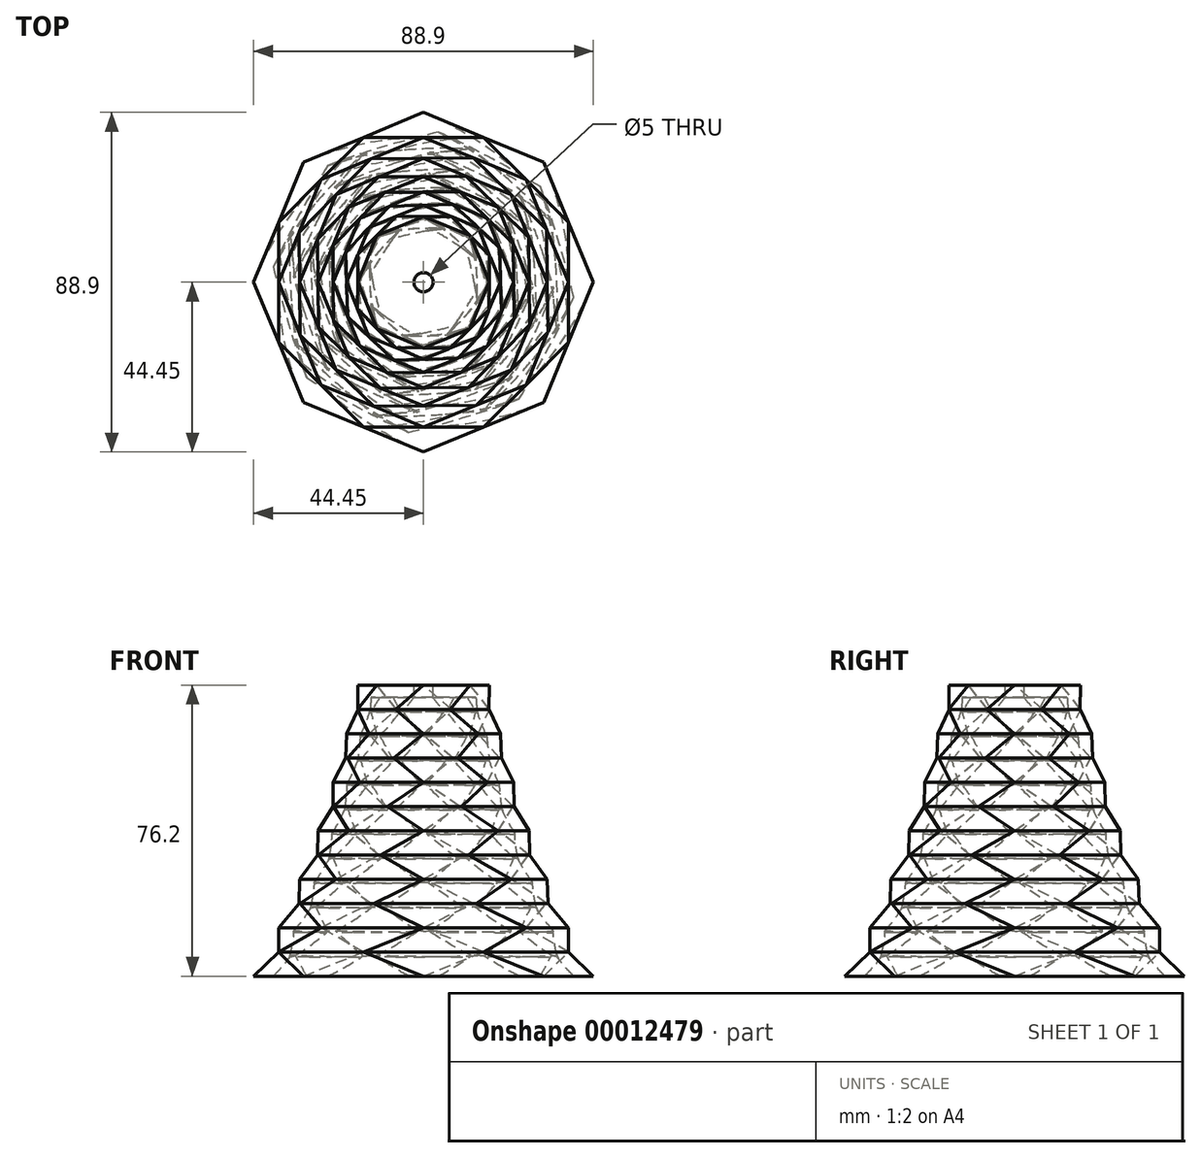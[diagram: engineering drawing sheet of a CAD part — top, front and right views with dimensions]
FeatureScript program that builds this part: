
annotation { "Feature Type Name" : "Feature", "Feature Type Description" : "" }
export const myFeature = defineFeature(function(context is Context, id is Id, definition is map)
    precondition{}
    {
        {
            var Q0;
            Q0=qCreatedBy(makeId("Top.planeOp"),FACE);
            var sketch = newSketch(context, id + "F0", { "sketchPlane" : qUnion([Q0])});
            skLineSegment(sketch, "E0.rect.bottom", {"start": v(88.9, -88.9) * mm, "end": v(-88.9, -88.9) * mm, "construction": true});
            skLineSegment(sketch, "E0.rect.top", {"start": v(88.9, 88.9) * mm, "end": v(-88.9, 88.9) * mm, "construction": true});
            skLineSegment(sketch, "E0.rect.left", {"start": v(88.9, -88.9) * mm, "end": v(88.9, 88.9) * mm, "construction": true});
            skLineSegment(sketch, "E0.rect.right", {"start": v(-88.9, -88.9) * mm, "end": v(-88.9, 88.9) * mm, "construction": true});
            skPoint(sketch, "E0.rect.middle", {"position": v(0, 0) * mm});
            skCircle(sketch, "E1.cCircle", {"center": v(0, 0) * mm, "radius": 88.9 * mm, "construction": true});
            skLineSegment(sketch, "E1.0", {"start": v(88.9, 0) * mm, "end": v(62.86, -62.86) * mm});
            skLineSegment(sketch, "E1.1", {"start": v(62.86, -62.86) * mm, "end": v(0, -88.9) * mm});
            skLineSegment(sketch, "E1.2", {"start": v(0, -88.9) * mm, "end": v(-62.86, -62.86) * mm});
            skLineSegment(sketch, "E1.3", {"start": v(-62.86, -62.86) * mm, "end": v(-88.9, 0) * mm});
            skLineSegment(sketch, "E1.4", {"start": v(-88.9, 0) * mm, "end": v(-62.86, 62.86) * mm});
            skLineSegment(sketch, "E1.5", {"start": v(-62.86, 62.86) * mm, "end": v(0, 88.9) * mm});
            skLineSegment(sketch, "E1.6", {"start": v(0, 88.9) * mm, "end": v(62.86, 62.86) * mm});
            skLineSegment(sketch, "E1.7", {"start": v(62.86, 62.86) * mm, "end": v(88.9, 0) * mm});
            skSolve(sketch);
        }
        {
            var Q0;
            Q0=qCreatedBy(makeId("Top.planeOp"),FACE);
            cPlane(context, id + "F1", {"entities" : qUnion([Q0]), "cplaneType" : CPlaneType.OFFSET, "offset" : 12.7 * mm, "width" : 152.4 * mm, "height" : 152.4 * mm});
        }
        {
            var Q0;
            Q0=qCreatedBy(id+"F1.planeOp",FACE);
            var sketch = newSketch(context, id + "F2", { "sketchPlane" : qUnion([Q0])});
            skPoint(sketch, "E2.0", {"position": v(0, 0) * mm});
            skCircle(sketch, "E3.cCircle", {"center": v(0, 0) * mm, "radius": 82.13 * mm, "construction": true});
            skLineSegment(sketch, "E3.0", {"start": v(75.88, -31.43) * mm, "end": v(31.43, -75.88) * mm});
            skLineSegment(sketch, "E3.1", {"start": v(31.43, -75.88) * mm, "end": v(-31.43, -75.88) * mm});
            skLineSegment(sketch, "E3.2", {"start": v(-31.43, -75.88) * mm, "end": v(-75.88, -31.43) * mm});
            skLineSegment(sketch, "E3.3", {"start": v(-75.88, -31.43) * mm, "end": v(-75.88, 31.43) * mm});
            skLineSegment(sketch, "E3.4", {"start": v(-75.88, 31.43) * mm, "end": v(-31.43, 75.88) * mm});
            skLineSegment(sketch, "E3.5", {"start": v(-31.43, 75.88) * mm, "end": v(31.43, 75.88) * mm});
            skLineSegment(sketch, "E3.6", {"start": v(31.43, 75.88) * mm, "end": v(75.88, 31.43) * mm});
            skLineSegment(sketch, "E3.7", {"start": v(75.88, 31.43) * mm, "end": v(75.88, -31.43) * mm});
            skSolve(sketch);
        }
        {
            var Q0;
            Q0=makeQuery(id+"F0.imprint","IMPRINT",FACE,{"disambiguationData":[TD([[makeQuery(id+"F0.imprint","IMPRINT",EDGE,{"derivedFrom":sQuery(id+"F0.wireOp",EDGE,"E1.0")}),-1.0]])]});
            var Q1;
            Q1=makeQuery(id+"F2.imprint","IMPRINT",FACE,{"disambiguationData":[TD([[makeQuery(id+"F2.imprint","IMPRINT",EDGE,{"derivedFrom":sQuery(id+"F2.wireOp",EDGE,"E3.0")}),-1.0]])]});
            loft(context, id + "F3", {"sheetProfilesArray" : [{ "sheetProfileEntities" : qUnion([Q0]) }, { "sheetProfileEntities" : qUnion([Q1]) }]});
        }
        {
            var Q0;
            Q0=qCreatedBy(id+"F1.planeOp",FACE);
            cPlane(context, id + "F4", {"entities" : qUnion([Q0]), "cplaneType" : CPlaneType.OFFSET, "offset" : 12.7 * mm, "width" : 152.4 * mm, "height" : 152.4 * mm});
        }
        {
            var Q0;
            Q0=qCreatedBy(id+"F4.planeOp",FACE);
            var sketch = newSketch(context, id + "F5", { "sketchPlane" : qUnion([Q0])});
            skFitSpline(sketch, "E4.0", {"points": [v(75.88, -31.43) * mm, v(75.88, -10.48) * mm, v(75.88, 10.48) * mm, v(75.88, 31.43) * mm]});
            skCircle(sketch, "E5.cCircle", {"center": v(0, 0) * mm, "radius": 75.88 * mm, "construction": true});
            skLineSegment(sketch, "E5.0", {"start": v(75.88, 0) * mm, "end": v(53.66, -53.66) * mm});
            skLineSegment(sketch, "E5.1", {"start": v(53.66, -53.66) * mm, "end": v(0, -75.88) * mm});
            skLineSegment(sketch, "E5.2", {"start": v(0, -75.88) * mm, "end": v(-53.66, -53.66) * mm});
            skLineSegment(sketch, "E5.3", {"start": v(-53.66, -53.66) * mm, "end": v(-75.88, 0) * mm});
            skLineSegment(sketch, "E5.4", {"start": v(-75.88, 0) * mm, "end": v(-53.66, 53.66) * mm});
            skLineSegment(sketch, "E5.5", {"start": v(-53.66, 53.66) * mm, "end": v(0, 75.88) * mm});
            skLineSegment(sketch, "E5.6", {"start": v(0, 75.88) * mm, "end": v(53.66, 53.66) * mm});
            skLineSegment(sketch, "E5.7", {"start": v(53.66, 53.66) * mm, "end": v(75.88, 0) * mm});
            skSolve(sketch);
        }
        {
            var Q1;
            Q1=makeQuery(id+"F3.opLoft","CAP_FACE",FACE,{"disambiguationData":[OSD([makeQuery(id+"F2.imprint","IMPRINT",FACE,{"disambiguationData":[TD([[makeQuery(id+"F2.imprint","IMPRINT",EDGE,{"derivedFrom":sQuery(id+"F2.wireOp",EDGE,"E3.0")}),-1.0]])]})])],"isStart":true});
            var Q2;
            Q2=makeQuery(id+"F5.imprint","IMPRINT",FACE,{"disambiguationData":[TD([[makeQuery(id+"F5.imprint","IMPRINT",EDGE,{"derivedFrom":sQuery(id+"F5.wireOp",EDGE,"E5.0")}),-1.0]])]});
            loft(context, id + "F6", {"operationType" : NewBodyOperationType.ADD, "sheetProfilesArray" : [{ "sheetProfileEntities" : qUnion([Q1]) }, { "sheetProfileEntities" : qUnion([Q2]) }]});
        }
        {
            var Q0;
            Q0=qCreatedBy(id+"F4.planeOp",FACE);
            cPlane(context, id + "F7", {"entities" : qUnion([Q0]), "cplaneType" : CPlaneType.OFFSET, "offset" : 12.7 * mm, "width" : 152.4 * mm, "height" : 152.4 * mm});
        }
        {
            var Q0;
            Q0=qCreatedBy(id+"F7.planeOp",FACE);
            var sketch = newSketch(context, id + "F8", { "sketchPlane" : qUnion([Q0])});
            skCircle(sketch, "E6.cCircle", {"center": v(0, 0) * mm, "radius": 70.1 * mm, "construction": true});
            skLineSegment(sketch, "E6.0", {"start": v(64.47, 27.56) * mm, "end": v(65.07, -26.1) * mm});
            skLineSegment(sketch, "E6.1", {"start": v(65.07, -26.1) * mm, "end": v(27.56, -64.47) * mm});
            skLineSegment(sketch, "E6.2", {"start": v(27.56, -64.47) * mm, "end": v(-26.1, -65.07) * mm});
            skLineSegment(sketch, "E6.3", {"start": v(-26.1, -65.07) * mm, "end": v(-64.47, -27.56) * mm});
            skLineSegment(sketch, "E6.4", {"start": v(-64.47, -27.56) * mm, "end": v(-65.07, 26.1) * mm});
            skLineSegment(sketch, "E6.5", {"start": v(-65.07, 26.1) * mm, "end": v(-27.56, 64.47) * mm});
            skLineSegment(sketch, "E6.6", {"start": v(-27.56, 64.47) * mm, "end": v(26.1, 65.07) * mm});
            skLineSegment(sketch, "E6.7", {"start": v(26.1, 65.07) * mm, "end": v(64.47, 27.56) * mm});
            skSolve(sketch);
        }
        {
            var Q1;
            Q1=makeQuery(id+"F6.opLoft","CAP_FACE",FACE,{"disambiguationData":[OSD([makeQuery(id+"F5.imprint","IMPRINT",FACE,{"disambiguationData":[TD([[makeQuery(id+"F5.imprint","IMPRINT",EDGE,{"derivedFrom":sQuery(id+"F5.wireOp",EDGE,"E5.0")}),-1.0]])]})])],"isStart":true});
            var Q2;
            Q2=makeQuery(id+"F8.imprint","IMPRINT",FACE,{"disambiguationData":[TD([[makeQuery(id+"F8.imprint","IMPRINT",EDGE,{"derivedFrom":sQuery(id+"F8.wireOp",EDGE,"E6.0")}),-1.0]])]});
            loft(context, id + "F9", {"operationType" : NewBodyOperationType.ADD, "sheetProfilesArray" : [{ "sheetProfileEntities" : qUnion([Q1]) }, { "sheetProfileEntities" : qUnion([Q2]) }]});
        }
        {
            var Q0;
            Q0=qCreatedBy(id+"F7.planeOp",FACE);
            cPlane(context, id + "F10", {"entities" : qUnion([Q0]), "cplaneType" : CPlaneType.OFFSET, "offset" : 12.7 * mm, "width" : 152.4 * mm, "height" : 152.4 * mm});
        }
        {
            var Q0;
            Q0=qCreatedBy(id+"F10.planeOp",FACE);
            var sketch = newSketch(context, id + "F11", { "sketchPlane" : qUnion([Q0])});
            skCircle(sketch, "E7.cCircle", {"center": v(0, 0) * mm, "radius": 64.78 * mm, "construction": true});
            skLineSegment(sketch, "E7.0", {"start": v(-64.78, 0) * mm, "end": v(-45.8, 45.8) * mm});
            skLineSegment(sketch, "E7.1", {"start": v(-45.8, 45.8) * mm, "end": v(0, 64.78) * mm});
            skLineSegment(sketch, "E7.2", {"start": v(0, 64.78) * mm, "end": v(45.8, 45.8) * mm});
            skLineSegment(sketch, "E7.3", {"start": v(45.8, 45.8) * mm, "end": v(64.78, 0) * mm});
            skLineSegment(sketch, "E7.4", {"start": v(64.78, 0) * mm, "end": v(45.8, -45.8) * mm});
            skLineSegment(sketch, "E7.5", {"start": v(45.8, -45.8) * mm, "end": v(0, -64.78) * mm});
            skLineSegment(sketch, "E7.6", {"start": v(0, -64.78) * mm, "end": v(-45.8, -45.8) * mm});
            skLineSegment(sketch, "E7.7", {"start": v(-45.8, -45.8) * mm, "end": v(-64.78, 0) * mm});
            skSolve(sketch);
        }
        {
            var Q1;
            Q1=makeQuery(id+"F9.opLoft","CAP_FACE",FACE,{"disambiguationData":[OSD([makeQuery(id+"F8.imprint","IMPRINT",FACE,{"disambiguationData":[TD([[makeQuery(id+"F8.imprint","IMPRINT",EDGE,{"derivedFrom":sQuery(id+"F8.wireOp",EDGE,"E6.0")}),-1.0]])]})])],"isStart":true});
            var Q2;
            Q2=makeQuery(id+"F11.imprint","IMPRINT",FACE,{"disambiguationData":[TD([[makeQuery(id+"F11.imprint","IMPRINT",EDGE,{"derivedFrom":sQuery(id+"F11.wireOp",EDGE,"E7.0")}),-1.0]])]});
            loft(context, id + "F12", {"operationType" : NewBodyOperationType.ADD, "sheetProfilesArray" : [{ "sheetProfileEntities" : qUnion([Q1]) }, { "sheetProfileEntities" : qUnion([Q2]) }]});
        }
        {
            var Q0;
            Q0=qCreatedBy(id+"F10.planeOp",FACE);
            cPlane(context, id + "F13", {"entities" : qUnion([Q0]), "cplaneType" : CPlaneType.OFFSET, "offset" : 12.7 * mm, "width" : 152.4 * mm, "height" : 152.4 * mm});
        }
        {
            var Q0;
            Q0=qCreatedBy(id+"F13.planeOp",FACE);
            var sketch = newSketch(context, id + "F14", { "sketchPlane" : qUnion([Q0])});
            skFitSpline(sketch, "E8.0", {"points": [v(64.78, 0) * mm, v(58.45, 15.27) * mm, v(52.13, 30.54) * mm, v(45.8, 45.8) * mm]});
            skCircle(sketch, "E9.cCircle", {"center": v(0, 0) * mm, "radius": 59.85 * mm, "construction": true});
            skLineSegment(sketch, "E9.0", {"start": v(55.07, 23.43) * mm, "end": v(55.51, -22.37) * mm});
            skLineSegment(sketch, "E9.1", {"start": v(55.51, -22.37) * mm, "end": v(23.43, -55.07) * mm});
            skLineSegment(sketch, "E9.2", {"start": v(23.43, -55.07) * mm, "end": v(-22.37, -55.51) * mm});
            skLineSegment(sketch, "E9.3", {"start": v(-22.37, -55.51) * mm, "end": v(-55.07, -23.43) * mm});
            skLineSegment(sketch, "E9.4", {"start": v(-55.07, -23.43) * mm, "end": v(-55.51, 22.37) * mm});
            skLineSegment(sketch, "E9.5", {"start": v(-55.51, 22.37) * mm, "end": v(-23.43, 55.07) * mm});
            skLineSegment(sketch, "E9.6", {"start": v(-23.43, 55.07) * mm, "end": v(22.37, 55.51) * mm});
            skLineSegment(sketch, "E9.7", {"start": v(22.37, 55.51) * mm, "end": v(55.07, 23.43) * mm});
            skSolve(sketch);
        }
        {
            var Q1;
            Q1=makeQuery(id+"F12.opLoft","CAP_FACE",FACE,{"disambiguationData":[OSD([makeQuery(id+"F11.imprint","IMPRINT",FACE,{"disambiguationData":[TD([[makeQuery(id+"F11.imprint","IMPRINT",EDGE,{"derivedFrom":sQuery(id+"F11.wireOp",EDGE,"E7.0")}),-1.0]])]})])],"isStart":true});
            var Q2;
            Q2=makeQuery(id+"F14.imprint","IMPRINT",FACE,{"disambiguationData":[TD([[makeQuery(id+"F14.imprint","IMPRINT",EDGE,{"derivedFrom":sQuery(id+"F14.wireOp",EDGE,"E9.0")}),-1.0]])]});
            loft(context, id + "F15", {"operationType" : NewBodyOperationType.ADD, "sheetProfilesArray" : [{ "sheetProfileEntities" : qUnion([Q1]) }, { "sheetProfileEntities" : qUnion([Q2]) }]});
        }
        {
            var Q0;
            Q0=qCreatedBy(id+"F13.planeOp",FACE);
            cPlane(context, id + "F16", {"entities" : qUnion([Q0]), "cplaneType" : CPlaneType.OFFSET, "offset" : 12.7 * mm, "width" : 152.4 * mm, "height" : 152.4 * mm});
        }
        {
            var Q0;
            Q0=qCreatedBy(id+"F16.planeOp",FACE);
            var sketch = newSketch(context, id + "F17", { "sketchPlane" : qUnion([Q0])});
            skFitSpline(sketch, "E10.0", {"points": [v(55.51, -22.37) * mm, v(55.36, -7.1) * mm, v(55.22, 8.17) * mm, v(55.07, 23.43) * mm]});
            skCircle(sketch, "E11.cCircle", {"center": v(0, 0) * mm, "radius": 55.3 * mm, "construction": true});
            skLineSegment(sketch, "E11.0", {"start": v(55.3, 0) * mm, "end": v(39.1, -39.1) * mm});
            skLineSegment(sketch, "E11.1", {"start": v(39.1, -39.1) * mm, "end": v(0, -55.3) * mm});
            skLineSegment(sketch, "E11.2", {"start": v(0, -55.3) * mm, "end": v(-39.1, -39.1) * mm});
            skLineSegment(sketch, "E11.3", {"start": v(-39.1, -39.1) * mm, "end": v(-55.3, 0) * mm});
            skLineSegment(sketch, "E11.4", {"start": v(-55.3, 0) * mm, "end": v(-39.1, 39.1) * mm});
            skLineSegment(sketch, "E11.5", {"start": v(-39.1, 39.1) * mm, "end": v(0, 55.3) * mm});
            skLineSegment(sketch, "E11.6", {"start": v(0, 55.3) * mm, "end": v(39.1, 39.1) * mm});
            skLineSegment(sketch, "E11.7", {"start": v(39.1, 39.1) * mm, "end": v(55.3, 0) * mm});
            skSolve(sketch);
        }
        {
            var Q1;
            Q1=makeQuery(id+"F15.opLoft","CAP_FACE",FACE,{"disambiguationData":[OSD([makeQuery(id+"F14.imprint","IMPRINT",FACE,{"disambiguationData":[TD([[makeQuery(id+"F14.imprint","IMPRINT",EDGE,{"derivedFrom":sQuery(id+"F14.wireOp",EDGE,"E9.0")}),-1.0]])]})])],"isStart":true});
            var Q2;
            Q2=makeQuery(id+"F17.imprint","IMPRINT",FACE,{"disambiguationData":[TD([[makeQuery(id+"F17.imprint","IMPRINT",EDGE,{"derivedFrom":sQuery(id+"F17.wireOp",EDGE,"E11.0")}),-1.0]])]});
            loft(context, id + "F18", {"operationType" : NewBodyOperationType.ADD, "sheetProfilesArray" : [{ "sheetProfileEntities" : qUnion([Q1]) }, { "sheetProfileEntities" : qUnion([Q2]) }]});
        }
        {
            var Q0;
            Q0=qCreatedBy(id+"F16.planeOp",FACE);
            cPlane(context, id + "F19", {"entities" : qUnion([Q0]), "cplaneType" : CPlaneType.OFFSET, "offset" : 12.7 * mm, "width" : 152.4 * mm, "height" : 152.4 * mm});
        }
        {
            var Q0;
            Q0=qCreatedBy(id+"F19.planeOp",FACE);
            var sketch = newSketch(context, id + "F20", { "sketchPlane" : qUnion([Q0])});
            skCircle(sketch, "E12.cCircle", {"center": v(0, 0) * mm, "radius": 51.09 * mm, "construction": true});
            skLineSegment(sketch, "E12.0", {"start": v(46.97, 20.1) * mm, "end": v(47.43, -19) * mm});
            skLineSegment(sketch, "E12.1", {"start": v(47.43, -19) * mm, "end": v(20.1, -46.97) * mm});
            skLineSegment(sketch, "E12.2", {"start": v(20.1, -46.97) * mm, "end": v(-19, -47.43) * mm});
            skLineSegment(sketch, "E12.3", {"start": v(-19, -47.43) * mm, "end": v(-46.97, -20.1) * mm});
            skLineSegment(sketch, "E12.4", {"start": v(-46.97, -20.1) * mm, "end": v(-47.43, 19) * mm});
            skLineSegment(sketch, "E12.5", {"start": v(-47.43, 19) * mm, "end": v(-20.1, 46.97) * mm});
            skLineSegment(sketch, "E12.6", {"start": v(-20.1, 46.97) * mm, "end": v(19, 47.43) * mm});
            skLineSegment(sketch, "E12.7", {"start": v(19, 47.43) * mm, "end": v(46.97, 20.1) * mm});
            skSolve(sketch);
        }
        {
            var Q1;
            Q1=makeQuery(id+"F18.opLoft","CAP_FACE",FACE,{"disambiguationData":[OSD([makeQuery(id+"F17.imprint","IMPRINT",FACE,{"disambiguationData":[TD([[makeQuery(id+"F17.imprint","IMPRINT",EDGE,{"derivedFrom":sQuery(id+"F17.wireOp",EDGE,"E11.0")}),-1.0]])]})])],"isStart":true});
            var Q2;
            Q2=makeQuery(id+"F20.imprint","IMPRINT",FACE,{"disambiguationData":[TD([[makeQuery(id+"F20.imprint","IMPRINT",EDGE,{"derivedFrom":sQuery(id+"F20.wireOp",EDGE,"E12.0")}),-1.0]])]});
            loft(context, id + "F21", {"operationType" : NewBodyOperationType.ADD, "sheetProfilesArray" : [{ "sheetProfileEntities" : qUnion([Q1]) }, { "sheetProfileEntities" : qUnion([Q2]) }]});
        }
        {
            var Q0;
            Q0=qCreatedBy(id+"F19.planeOp",FACE);
            cPlane(context, id + "F22", {"entities" : qUnion([Q0]), "cplaneType" : CPlaneType.OFFSET, "offset" : 12.7 * mm, "width" : 152.4 * mm, "height" : 152.4 * mm});
        }
        {
            var Q0;
            Q0=qCreatedBy(id+"F22.planeOp",FACE);
            var sketch = newSketch(context, id + "F23", { "sketchPlane" : qUnion([Q0])});
            skCircle(sketch, "E13.cCircle", {"center": v(0, 0) * mm, "radius": 47.2 * mm, "construction": true});
            skLineSegment(sketch, "E13.0", {"start": v(47.2, 0) * mm, "end": v(33.38, -33.38) * mm});
            skLineSegment(sketch, "E13.1", {"start": v(33.38, -33.38) * mm, "end": v(0, -47.2) * mm});
            skLineSegment(sketch, "E13.2", {"start": v(0, -47.2) * mm, "end": v(-33.38, -33.38) * mm});
            skLineSegment(sketch, "E13.3", {"start": v(-33.38, -33.38) * mm, "end": v(-47.2, 0) * mm});
            skLineSegment(sketch, "E13.4", {"start": v(-47.2, 0) * mm, "end": v(-33.38, 33.38) * mm});
            skLineSegment(sketch, "E13.5", {"start": v(-33.38, 33.38) * mm, "end": v(0, 47.2) * mm});
            skLineSegment(sketch, "E13.6", {"start": v(0, 47.2) * mm, "end": v(33.38, 33.38) * mm});
            skLineSegment(sketch, "E13.7", {"start": v(33.38, 33.38) * mm, "end": v(47.2, 0) * mm});
            skSolve(sketch);
        }
        {
            var Q1;
            Q1=makeQuery(id+"F21.opLoft","CAP_FACE",FACE,{"disambiguationData":[OSD([makeQuery(id+"F20.imprint","IMPRINT",FACE,{"disambiguationData":[TD([[makeQuery(id+"F20.imprint","IMPRINT",EDGE,{"derivedFrom":sQuery(id+"F20.wireOp",EDGE,"E12.0")}),-1.0]])]})])],"isStart":true});
            var Q2;
            Q2=makeQuery(id+"F23.imprint","IMPRINT",FACE,{"disambiguationData":[TD([[makeQuery(id+"F23.imprint","IMPRINT",EDGE,{"derivedFrom":sQuery(id+"F23.wireOp",EDGE,"E13.0")}),-1.0]])]});
            loft(context, id + "F24", {"operationType" : NewBodyOperationType.ADD, "sheetProfilesArray" : [{ "sheetProfileEntities" : qUnion([Q1]) }, { "sheetProfileEntities" : qUnion([Q2]) }]});
        }
        {
            var Q0;
            Q0=qCreatedBy(id+"F22.planeOp",FACE);
            cPlane(context, id + "F25", {"entities" : qUnion([Q0]), "cplaneType" : CPlaneType.OFFSET, "offset" : 12.7 * mm, "width" : 152.4 * mm, "height" : 152.4 * mm});
        }
        {
            var Q0;
            Q0=qCreatedBy(id+"F25.planeOp",FACE);
            var sketch = newSketch(context, id + "F26", { "sketchPlane" : qUnion([Q0])});
            skCircle(sketch, "E14.cCircle", {"center": v(0, 0) * mm, "radius": 43.63 * mm, "construction": true});
            skLineSegment(sketch, "E14.0", {"start": v(39.79, 17.9) * mm, "end": v(40.8, -15.47) * mm});
            skLineSegment(sketch, "E14.1", {"start": v(40.8, -15.47) * mm, "end": v(17.9, -39.79) * mm});
            skLineSegment(sketch, "E14.2", {"start": v(17.9, -39.79) * mm, "end": v(-15.47, -40.8) * mm});
            skLineSegment(sketch, "E14.3", {"start": v(-15.47, -40.8) * mm, "end": v(-39.79, -17.9) * mm});
            skLineSegment(sketch, "E14.4", {"start": v(-39.79, -17.9) * mm, "end": v(-40.8, 15.47) * mm});
            skLineSegment(sketch, "E14.5", {"start": v(-40.8, 15.47) * mm, "end": v(-17.9, 39.79) * mm});
            skLineSegment(sketch, "E14.6", {"start": v(-17.9, 39.79) * mm, "end": v(15.47, 40.8) * mm});
            skLineSegment(sketch, "E14.7", {"start": v(15.47, 40.8) * mm, "end": v(39.79, 17.9) * mm});
            skSolve(sketch);
        }
        {
            var Q1;
            Q1=makeQuery(id+"F24.opLoft","CAP_FACE",FACE,{"disambiguationData":[OSD([makeQuery(id+"F23.imprint","IMPRINT",FACE,{"disambiguationData":[TD([[makeQuery(id+"F23.imprint","IMPRINT",EDGE,{"derivedFrom":sQuery(id+"F23.wireOp",EDGE,"E13.0")}),-1.0]])]})])],"isStart":true});
            var Q2;
            Q2=makeQuery(id+"F26.imprint","IMPRINT",FACE,{"disambiguationData":[TD([[makeQuery(id+"F26.imprint","IMPRINT",EDGE,{"derivedFrom":sQuery(id+"F26.wireOp",EDGE,"E14.0")}),-1.0]])]});
            loft(context, id + "F27", {"operationType" : NewBodyOperationType.ADD, "sheetProfilesArray" : [{ "sheetProfileEntities" : qUnion([Q1]) }, { "sheetProfileEntities" : qUnion([Q2]) }]});
        }
        {
            var Q0;
            Q0=qCreatedBy(id+"F25.planeOp",FACE);
            cPlane(context, id + "F28", {"entities" : qUnion([Q0]), "cplaneType" : CPlaneType.OFFSET, "offset" : 12.7 * mm, "width" : 152.4 * mm, "height" : 152.4 * mm});
        }
        {
            var Q0;
            Q0=qCreatedBy(id+"F28.planeOp",FACE);
            var sketch = newSketch(context, id + "F29", { "sketchPlane" : qUnion([Q0])});
            skCircle(sketch, "E15.cCircle", {"center": v(0, 0) * mm, "radius": 40.33 * mm, "construction": true});
            skLineSegment(sketch, "E15.0", {"start": v(40.33, 0) * mm, "end": v(28.52, -28.52) * mm});
            skLineSegment(sketch, "E15.1", {"start": v(28.52, -28.52) * mm, "end": v(0, -40.33) * mm});
            skLineSegment(sketch, "E15.2", {"start": v(0, -40.33) * mm, "end": v(-28.52, -28.52) * mm});
            skLineSegment(sketch, "E15.3", {"start": v(-28.52, -28.52) * mm, "end": v(-40.33, 0) * mm});
            skLineSegment(sketch, "E15.4", {"start": v(-40.33, 0) * mm, "end": v(-28.52, 28.52) * mm});
            skLineSegment(sketch, "E15.5", {"start": v(-28.52, 28.52) * mm, "end": v(0, 40.33) * mm});
            skLineSegment(sketch, "E15.6", {"start": v(0, 40.33) * mm, "end": v(28.52, 28.52) * mm});
            skLineSegment(sketch, "E15.7", {"start": v(28.52, 28.52) * mm, "end": v(40.33, 0) * mm});
            skSolve(sketch);
        }
        {
            var Q1;
            Q1=makeQuery(id+"F27.opLoft","CAP_FACE",FACE,{"disambiguationData":[OSD([makeQuery(id+"F26.imprint","IMPRINT",FACE,{"disambiguationData":[TD([[makeQuery(id+"F26.imprint","IMPRINT",EDGE,{"derivedFrom":sQuery(id+"F26.wireOp",EDGE,"E14.0")}),-1.0]])]})])],"isStart":true});
            var Q2;
            Q2=makeQuery(id+"F29.imprint","IMPRINT",FACE,{"disambiguationData":[TD([[makeQuery(id+"F29.imprint","IMPRINT",EDGE,{"derivedFrom":sQuery(id+"F29.wireOp",EDGE,"E15.0")}),-1.0]])]});
            loft(context, id + "F30", {"operationType" : NewBodyOperationType.ADD, "sheetProfilesArray" : [{ "sheetProfileEntities" : qUnion([Q1]) }, { "sheetProfileEntities" : qUnion([Q2]) }]});
        }
        {
            var Q0;
            Q0=qCreatedBy(id+"F28.planeOp",FACE);
            cPlane(context, id + "F31", {"entities" : qUnion([Q0]), "cplaneType" : CPlaneType.OFFSET, "offset" : 12.7 * mm, "width" : 152.4 * mm, "height" : 152.4 * mm});
        }
        {
            var Q0;
            Q0=qCreatedBy(id+"F31.planeOp",FACE);
            var sketch = newSketch(context, id + "F32", { "sketchPlane" : qUnion([Q0])});
            skFitSpline(sketch, "E16.0", {"points": [v(-40.33, 0) * mm, v(-36.4, -9.5) * mm, v(-32.45, -19.01) * mm, v(-28.52, -28.52) * mm]});
            skCircle(sketch, "E17.cCircle", {"center": v(0, 0) * mm, "radius": 37.26 * mm, "construction": true});
            skLineSegment(sketch, "E17.0", {"start": v(-34.53, -14) * mm, "end": v(-34.31, 14.53) * mm});
            skLineSegment(sketch, "E17.1", {"start": v(-34.31, 14.53) * mm, "end": v(-14, 34.53) * mm});
            skLineSegment(sketch, "E17.2", {"start": v(-14, 34.53) * mm, "end": v(14.53, 34.31) * mm});
            skLineSegment(sketch, "E17.3", {"start": v(14.53, 34.31) * mm, "end": v(34.53, 14) * mm});
            skLineSegment(sketch, "E17.4", {"start": v(34.53, 14) * mm, "end": v(34.31, -14.53) * mm});
            skLineSegment(sketch, "E17.5", {"start": v(34.31, -14.53) * mm, "end": v(14, -34.53) * mm});
            skLineSegment(sketch, "E17.6", {"start": v(14, -34.53) * mm, "end": v(-14.53, -34.31) * mm});
            skLineSegment(sketch, "E17.7", {"start": v(-14.53, -34.31) * mm, "end": v(-34.53, -14) * mm});
            skSolve(sketch);
        }
        {
            var Q1;
            Q1=makeQuery(id+"F30.opLoft","CAP_FACE",FACE,{"disambiguationData":[OSD([makeQuery(id+"F29.imprint","IMPRINT",FACE,{"disambiguationData":[TD([[makeQuery(id+"F29.imprint","IMPRINT",EDGE,{"derivedFrom":sQuery(id+"F29.wireOp",EDGE,"E15.0")}),-1.0]])]})])],"isStart":true});
            var Q2;
            Q2=makeQuery(id+"F32.imprint","IMPRINT",FACE,{"disambiguationData":[TD([[makeQuery(id+"F32.imprint","IMPRINT",EDGE,{"derivedFrom":sQuery(id+"F32.wireOp",EDGE,"E17.0")}),-1.0]])]});
            var Q3;
            Q3=makeQuery(id+"F30.opLoft","MID_CAP_VERTEX",VERTEX,{"disambiguationData":[OSD([sQuery(id+"F29.wireOp",EDGE,"E15.0"),sQuery(id+"F29.wireOp",EDGE,"E15.1")])],"capPos":1.0});
            var Q4;
            Q4=sQuery(id+"F32.wireOp",VERTEX,"E17.6.start");
            loft(context, id + "F33", {"operationType" : NewBodyOperationType.ADD, "sheetProfilesArray" : [{ "sheetProfileEntities" : qUnion([Q1]) }, { "sheetProfileEntities" : qUnion([Q2]) }], "matchConnections" : true, "connections" : [{ "connectionEntities" : qUnion([Q3, Q4]), "connectionEdgeQueries" : qUnion([]), "connectionEdgeParameters" : [] }]});
        }
        {
            var Q0;
            Q0=qCreatedBy(id+"F31.planeOp",FACE);
            cPlane(context, id + "F34", {"entities" : qUnion([Q0]), "cplaneType" : CPlaneType.OFFSET, "offset" : 12.7 * mm, "width" : 152.4 * mm, "height" : 152.4 * mm});
        }
        {
            var Q0;
            Q0=qCreatedBy(id+"F34.planeOp",FACE);
            var sketch = newSketch(context, id + "F35", { "sketchPlane" : qUnion([Q0])});
            skCircle(sketch, "E18.cCircle", {"center": v(0, 0) * mm, "radius": 34.42 * mm, "construction": true});
            skLineSegment(sketch, "E18.0", {"start": v(-34.42, 0) * mm, "end": v(-24.34, 24.34) * mm});
            skLineSegment(sketch, "E18.1", {"start": v(-24.34, 24.34) * mm, "end": v(0, 34.42) * mm});
            skLineSegment(sketch, "E18.2", {"start": v(0, 34.42) * mm, "end": v(24.34, 24.34) * mm});
            skLineSegment(sketch, "E18.3", {"start": v(24.34, 24.34) * mm, "end": v(34.42, 0) * mm});
            skLineSegment(sketch, "E18.4", {"start": v(34.42, 0) * mm, "end": v(24.34, -24.34) * mm});
            skLineSegment(sketch, "E18.5", {"start": v(24.34, -24.34) * mm, "end": v(0, -34.42) * mm});
            skLineSegment(sketch, "E18.6", {"start": v(0, -34.42) * mm, "end": v(-24.34, -24.34) * mm});
            skLineSegment(sketch, "E18.7", {"start": v(-24.34, -24.34) * mm, "end": v(-34.42, 0) * mm});
            skSolve(sketch);
        }
        {
            var Q1;
            Q1=makeQuery(id+"F33.opLoft","CAP_FACE",FACE,{"disambiguationData":[OSD([makeQuery(id+"F32.imprint","IMPRINT",FACE,{"disambiguationData":[TD([[makeQuery(id+"F32.imprint","IMPRINT",EDGE,{"derivedFrom":sQuery(id+"F32.wireOp",EDGE,"E17.0")}),-1.0]])]})])],"isStart":true});
            var Q2;
            Q2=makeQuery(id+"F35.imprint","IMPRINT",FACE,{"disambiguationData":[TD([[makeQuery(id+"F35.imprint","IMPRINT",EDGE,{"derivedFrom":sQuery(id+"F35.wireOp",EDGE,"E18.0")}),-1.0]])]});
            var Q3;
            Q3=makeQuery(id+"F33.opLoft","MID_CAP_VERTEX",VERTEX,{"disambiguationData":[OSD([sQuery(id+"F32.wireOp",EDGE,"E17.6"),sQuery(id+"F32.wireOp",EDGE,"E17.7")])],"capPos":1.0});
            var Q4;
            Q4=sQuery(id+"F35.wireOp",VERTEX,"E18.6.start");
            loft(context, id + "F36", {"operationType" : NewBodyOperationType.ADD, "sheetProfilesArray" : [{ "sheetProfileEntities" : qUnion([Q1]) }, { "sheetProfileEntities" : qUnion([Q2]) }], "matchConnections" : true, "connections" : [{ "connectionEntities" : qUnion([Q3, Q4]), "connectionEdgeQueries" : qUnion([]), "connectionEdgeParameters" : [] }]});
        }
        {
            var Q0;
            Q0=makeQuery(id+"F3.opLoft","CAP_FACE",FACE,{"disambiguationData":[OSD([makeQuery(id+"F0.imprint","IMPRINT",FACE,{"disambiguationData":[TD([[makeQuery(id+"F0.imprint","IMPRINT",EDGE,{"derivedFrom":sQuery(id+"F0.wireOp",EDGE,"E1.0")}),-1.0]])]})])],"isStart":true});
            shell(context, id + "F37", {"entities" : qUnion([Q0]), "thickness" : 6.35 * mm});
        }
        {
            var Q0;
            Q0=qCreatedBy(id+"F34.planeOp",FACE);
            var sketch = newSketch(context, id + "F38", { "sketchPlane" : qUnion([Q0])});
            skCircle(sketch, "E19", {"center": v(0, 0) * mm, "radius": 5 * mm});
            skSolve(sketch);
        }
        {
            var Q0;
            Q0=qSketchRegion(id+"F38",true);
            extrude(context, id + "F39", {"entities" : qUnion([Q0]), "operationType" : NewBodyOperationType.REMOVE, "oppositeDirection" : true, "depth" : 25 * mm});
        }
        {
            var Q0;
            Q0=makeQuery(id+"F3.opLoft","SWEPT_BODY",BODY,{"disambiguationData":[OSD([makeQuery(id+"F0.imprint","IMPRINT",FACE,{"disambiguationData":[TD([[makeQuery(id+"F0.imprint","IMPRINT",EDGE,{"derivedFrom":sQuery(id+"F0.wireOp",EDGE,"E1.0")}),-1.0]])]}),makeQuery(id+"F2.imprint","IMPRINT",FACE,{"disambiguationData":[TD([[makeQuery(id+"F2.imprint","IMPRINT",EDGE,{"derivedFrom":sQuery(id+"F2.wireOp",EDGE,"E3.0")}),-1.0]])]})])]});
            var Q1;
            Q1=sQuery(id+"F0.wireOp",VERTEX,"E0.rect.middle");
            transform(context, id + "F40", {"entities" : qUnion([Q0]), "transformType" : TransformType.SCALE_UNIFORMLY, "scale" : .5, "scalePoint" : qUnion([Q1]), "makeCopy" : false});
        }
    });
